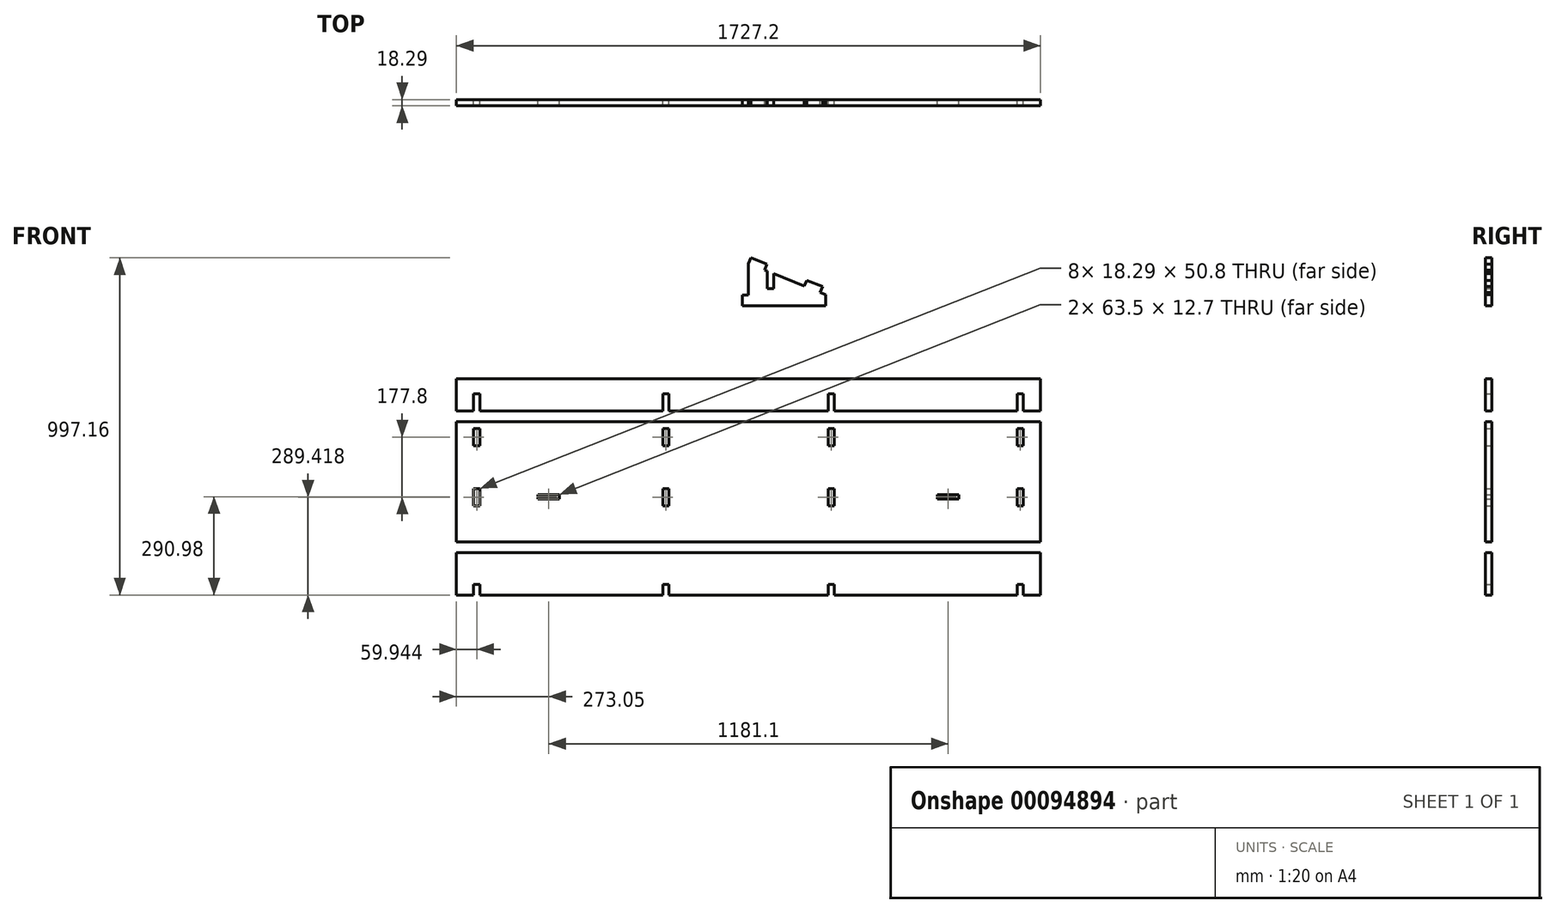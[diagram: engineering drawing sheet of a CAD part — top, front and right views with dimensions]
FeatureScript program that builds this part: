
annotation { "Feature Type Name" : "Feature", "Feature Type Description" : "" }
export const myFeature = defineFeature(function(context is Context, id is Id, definition is map)
    precondition{}
    {
        {
            var Q0;
            Q0=qCreatedBy(makeId("Front.planeOp"),FACE);
            var sketch = newSketch(context, id + "F0", { "sketchPlane" : qUnion([Q0])});
            skLineSegment(sketch, "E0.bottom", {"start": v(-863.6, 177.8) * mm, "end": v(863.6, 177.8) * mm});
            skLineSegment(sketch, "E0.top", {"start": v(-863.6, -177.8) * mm, "end": v(863.6, -177.8) * mm});
            skLineSegment(sketch, "E0.left", {"start": v(-863.6, 177.8) * mm, "end": v(-863.6, -177.8) * mm});
            skLineSegment(sketch, "E0.right", {"start": v(863.6, 177.8) * mm, "end": v(863.6, -177.8) * mm});
            skPoint(sketch, "E0.middle", {"position": v(0, 0) * mm});
            skLineSegment(sketch, "E1.bottom", {"start": v(-914.4, 444.5) * mm, "end": v(914.4, 444.5) * mm});
            skLineSegment(sketch, "E1.top", {"start": v(-914.4, 355.6) * mm, "end": v(914.4, 355.6) * mm});
            skLineSegment(sketch, "E1.left", {"start": v(-914.4, 444.5) * mm, "end": v(-914.4, 355.6) * mm});
            skLineSegment(sketch, "E1.right", {"start": v(914.4, 444.5) * mm, "end": v(914.4, 355.6) * mm});
            skPoint(sketch, "E2", {"position": v(0, 355.6) * mm});
            skLineSegment(sketch, "E3.bottom", {"start": v(0, 355.6) * mm, "end": v(-177.8, 355.6) * mm, "construction": true});
            skLineSegment(sketch, "E3.top", {"start": v(0, 406.4) * mm, "end": v(-177.8, 406.4) * mm, "construction": true});
            skLineSegment(sketch, "E3.left", {"start": v(0, 355.6) * mm, "end": v(0, 406.4) * mm, "construction": true});
            skLineSegment(sketch, "E3.right", {"start": v(-177.8, 355.6) * mm, "end": v(-177.8, 406.4) * mm, "construction": true});
            skLineSegment(sketch, "E4.MirrorCS", {"start": v(0, 406.4) * mm, "end": v(177.8, 406.4) * mm, "construction": true});
            skLineSegment(sketch, "E5.MirrorCS", {"start": v(177.8, 355.6) * mm, "end": v(177.8, 406.4) * mm, "construction": true});
            skLineSegment(sketch, "E6.bottom", {"start": v(177.8, 355.6) * mm, "end": v(482.6, 355.6) * mm});
            skLineSegment(sketch, "E6.top", {"start": v(177.8, 406.4) * mm, "end": v(482.6, 406.4) * mm});
            skLineSegment(sketch, "E6.left", {"start": v(177.8, 355.6) * mm, "end": v(177.8, 406.4) * mm});
            skLineSegment(sketch, "E6.right", {"start": v(482.6, 355.6) * mm, "end": v(482.6, 406.4) * mm});
            skLineSegment(sketch, "E7.bottom", {"start": v(-177.8, 355.6) * mm, "end": v(-482.6, 355.6) * mm});
            skLineSegment(sketch, "E7.top", {"start": v(-177.8, 406.4) * mm, "end": v(-482.6, 406.4) * mm});
            skLineSegment(sketch, "E7.left", {"start": v(-177.8, 355.6) * mm, "end": v(-177.8, 406.4) * mm});
            skLineSegment(sketch, "E7.right", {"start": v(-482.6, 355.6) * mm, "end": v(-482.6, 406.4) * mm});
            skLineSegment(sketch, "E8", {"start": v(0, 645.67) * mm, "end": v(0, 520.7) * mm});
            skLineSegment(sketch, "E9", {"start": v(0, 520.7) * mm, "end": v(228.6, 520.7) * mm});
            skLineSegment(sketch, "E10", {"start": v(228.6, 520.7) * mm, "end": v(228.6, 554.04) * mm});
            skLineSegment(sketch, "E11", {"start": v(228.6, 554.04) * mm, "end": v(0, 645.67) * mm});
            skLineSegment(sketch, "E12", {"start": v(-18.29, 653) * mm, "end": v(311.79, 520.7) * mm, "construction": true});
            skLineSegment(sketch, "E13", {"start": v(0, 645.67) * mm, "end": v(6.8, 662.64) * mm});
            skLineSegment(sketch, "E14", {"start": v(6.8, 662.64) * mm, "end": v(53.96, 643.74) * mm});
            skLineSegment(sketch, "E15", {"start": v(53.96, 643.74) * mm, "end": v(47.15, 626.77) * mm});
            skLineSegment(sketch, "E16.MirrorCS", {"start": v(219, 577.6) * mm, "end": v(171.84, 596.5) * mm});
            skLineSegment(sketch, "E17.MirrorCS", {"start": v(171.84, 596.5) * mm, "end": v(165.04, 579.52) * mm});
            skLineSegment(sketch, "E18.MirrorCS", {"start": v(212.2, 560.62) * mm, "end": v(219, 577.6) * mm});
            skLineSegment(sketch, "E19.0", {"start": v(-863.6, 158.1) * mm, "end": v(863.6, 158.1) * mm, "construction": true});
            skLineSegment(sketch, "E20.0", {"start": v(-863.6, -70.5) * mm, "end": v(863.6, -70.5) * mm, "construction": true});
            skLineSegment(sketch, "E21.bottom", {"start": v(-812.8, 158.1) * mm, "end": v(-794.51, 158.1) * mm});
            skLineSegment(sketch, "E21.top", {"start": v(-812.8, 107.3) * mm, "end": v(-794.51, 107.3) * mm});
            skLineSegment(sketch, "E21.left", {"start": v(-812.8, 158.1) * mm, "end": v(-812.8, 107.3) * mm});
            skLineSegment(sketch, "E21.right", {"start": v(-794.51, 158.1) * mm, "end": v(-794.51, 107.3) * mm});
            skLineSegment(sketch, "E22.0", {"start": v(-253.5, 158.1) * mm, "end": v(-253.5, 107.3) * mm});
            skLineSegment(sketch, "E23.bottom", {"start": v(-253.5, 158.1) * mm, "end": v(-235.2, 158.1) * mm});
            skLineSegment(sketch, "E23.top", {"start": v(-253.5, 107.3) * mm, "end": v(-235.2, 107.3) * mm});
            skLineSegment(sketch, "E23.right", {"start": v(-235.2, 158.1) * mm, "end": v(-235.2, 107.3) * mm});
            skLineSegment(sketch, "E24.MirrorCS", {"start": v(253.5, 107.3) * mm, "end": v(235.2, 107.3) * mm});
            skLineSegment(sketch, "E25.MirrorCS", {"start": v(253.5, 158.1) * mm, "end": v(235.2, 158.1) * mm});
            skLineSegment(sketch, "E26.MirrorCS", {"start": v(812.8, 158.1) * mm, "end": v(794.51, 158.1) * mm});
            skLineSegment(sketch, "E27.MirrorCS", {"start": v(812.8, 107.3) * mm, "end": v(794.51, 107.3) * mm});
            skLineSegment(sketch, "E28.MirrorCS", {"start": v(253.5, 158.1) * mm, "end": v(253.5, 107.3) * mm});
            skLineSegment(sketch, "E29.MirrorCS", {"start": v(794.51, 158.1) * mm, "end": v(794.51, 107.3) * mm});
            skLineSegment(sketch, "E30.MirrorCS", {"start": v(235.2, 158.1) * mm, "end": v(235.2, 107.3) * mm});
            skLineSegment(sketch, "E31.MirrorCS", {"start": v(812.8, 158.1) * mm, "end": v(812.8, 107.3) * mm});
            skLineSegment(sketch, "E32", {"start": v(0, 158.1) * mm, "end": v(0, -70.5) * mm, "construction": true});
            skLineSegment(sketch, "E33", {"start": v(0, 43.8) * mm, "end": v(301.25, 43.8) * mm, "construction": true});
            skLineSegment(sketch, "E34.MirrorCS", {"start": v(-253.5, -70.5) * mm, "end": v(-235.2, -70.5) * mm});
            skLineSegment(sketch, "E35.MirrorCS", {"start": v(-253.5, -19.7) * mm, "end": v(-235.2, -19.7) * mm});
            skLineSegment(sketch, "E36.MirrorCS", {"start": v(253.5, -70.5) * mm, "end": v(235.2, -70.5) * mm});
            skLineSegment(sketch, "E37.MirrorCS", {"start": v(253.5, -19.7) * mm, "end": v(235.2, -19.7) * mm});
            skLineSegment(sketch, "E38.MirrorCS", {"start": v(812.8, -19.7) * mm, "end": v(794.51, -19.7) * mm});
            skLineSegment(sketch, "E39.MirrorCS", {"start": v(-253.5, -70.5) * mm, "end": v(-253.5, -19.7) * mm});
            skLineSegment(sketch, "E40.MirrorCS", {"start": v(-812.8, -70.5) * mm, "end": v(-794.51, -70.5) * mm});
            skLineSegment(sketch, "E41.MirrorCS", {"start": v(812.8, -70.5) * mm, "end": v(794.51, -70.5) * mm});
            skLineSegment(sketch, "E42.MirrorCS", {"start": v(-812.8, -19.7) * mm, "end": v(-794.51, -19.7) * mm});
            skLineSegment(sketch, "E43.MirrorCS", {"start": v(253.5, -70.5) * mm, "end": v(253.5, -19.7) * mm});
            skLineSegment(sketch, "E44.MirrorCS", {"start": v(-794.51, -70.5) * mm, "end": v(-794.51, -19.7) * mm});
            skLineSegment(sketch, "E45.MirrorCS", {"start": v(235.2, -70.5) * mm, "end": v(235.2, -19.7) * mm});
            skLineSegment(sketch, "E46.MirrorCS", {"start": v(794.51, -70.5) * mm, "end": v(794.51, -19.7) * mm});
            skLineSegment(sketch, "E47.MirrorCS", {"start": v(-812.8, -70.5) * mm, "end": v(-812.8, -19.7) * mm});
            skLineSegment(sketch, "E48.MirrorCS", {"start": v(-235.2, -70.5) * mm, "end": v(-235.2, -19.7) * mm});
            skLineSegment(sketch, "E49.MirrorCS", {"start": v(812.8, -70.5) * mm, "end": v(812.8, -19.7) * mm});
            skLineSegment(sketch, "E50.bottom", {"start": v(55.86, 571.5) * mm, "end": v(74.14, 571.5) * mm});
            skLineSegment(sketch, "E50.top", {"start": v(55.86, 615.95) * mm, "end": v(74.14, 615.95) * mm, "construction": true});
            skLineSegment(sketch, "E50.left", {"start": v(55.86, 571.5) * mm, "end": v(55.86, 615.95) * mm});
            skLineSegment(sketch, "E50.right", {"start": v(74.14, 571.5) * mm, "end": v(74.14, 615.95) * mm});
            skLineSegment(sketch, "E51", {"start": v(55.86, 615.95) * mm, "end": v(55.86, 623.28) * mm});
            skLineSegment(sketch, "E52.bottom", {"start": v(-863.6, 209.55) * mm, "end": v(863.6, 209.55) * mm});
            skLineSegment(sketch, "E52.top", {"start": v(-863.6, 304.8) * mm, "end": v(863.6, 304.8) * mm});
            skLineSegment(sketch, "E52.left", {"start": v(-863.6, 209.55) * mm, "end": v(-863.6, 304.8) * mm});
            skLineSegment(sketch, "E52.right", {"start": v(863.6, 209.55) * mm, "end": v(863.6, 304.8) * mm});
            skLineSegment(sketch, "E53.bottom", {"start": v(-812.8, 209.55) * mm, "end": v(-794.51, 209.55) * mm});
            skLineSegment(sketch, "E53.top", {"start": v(-812.8, 260.35) * mm, "end": v(-794.51, 260.35) * mm});
            skLineSegment(sketch, "E53.left", {"start": v(-812.8, 209.55) * mm, "end": v(-812.8, 260.35) * mm});
            skLineSegment(sketch, "E53.right", {"start": v(-794.51, 209.55) * mm, "end": v(-794.51, 260.35) * mm});
            skLineSegment(sketch, "E54.bottom", {"start": v(-253.5, 209.55) * mm, "end": v(-235.2, 209.55) * mm});
            skLineSegment(sketch, "E54.top", {"start": v(-253.5, 260.35) * mm, "end": v(-235.2, 260.35) * mm});
            skLineSegment(sketch, "E54.left", {"start": v(-253.5, 209.55) * mm, "end": v(-253.5, 260.35) * mm});
            skLineSegment(sketch, "E54.right", {"start": v(-235.2, 209.55) * mm, "end": v(-235.2, 260.35) * mm});
            skLineSegment(sketch, "E55.MirrorCS", {"start": v(812.8, 209.55) * mm, "end": v(794.51, 209.55) * mm});
            skLineSegment(sketch, "E56.MirrorCS", {"start": v(235.2, 209.55) * mm, "end": v(235.2, 260.35) * mm});
            skLineSegment(sketch, "E57.MirrorCS", {"start": v(812.8, 260.35) * mm, "end": v(794.51, 260.35) * mm});
            skLineSegment(sketch, "E58.MirrorCS", {"start": v(253.5, 209.55) * mm, "end": v(253.5, 260.35) * mm});
            skLineSegment(sketch, "E59.MirrorCS", {"start": v(253.5, 260.35) * mm, "end": v(235.2, 260.35) * mm});
            skLineSegment(sketch, "E60.MirrorCS", {"start": v(253.5, 209.55) * mm, "end": v(235.2, 209.55) * mm});
            skLineSegment(sketch, "E61.MirrorCS", {"start": v(794.51, 209.55) * mm, "end": v(794.51, 260.35) * mm});
            skLineSegment(sketch, "E62.MirrorCS", {"start": v(812.8, 209.55) * mm, "end": v(812.8, 260.35) * mm});
            skLineSegment(sketch, "E63.bottom", {"start": v(0, 520.7) * mm, "end": v(-18.29, 520.7) * mm});
            skLineSegment(sketch, "E63.top", {"start": v(0, 552.45) * mm, "end": v(-18.29, 552.45) * mm});
            skLineSegment(sketch, "E63.left", {"start": v(0, 520.7) * mm, "end": v(0, 552.45) * mm});
            skLineSegment(sketch, "E63.right", {"start": v(-18.29, 520.7) * mm, "end": v(-18.29, 552.45) * mm});
            skLineSegment(sketch, "E64", {"start": v(0, 583.18) * mm, "end": v(305.15, 583.18) * mm, "construction": true});
            skLineSegment(sketch, "E65", {"start": v(205.05, 583.18) * mm, "end": v(198.24, 566.2) * mm, "construction": true});
            skLineSegment(sketch, "E66.0", {"start": v(188.07, 589.99) * mm, "end": v(181.27, 573.01) * mm});
            skLineSegment(sketch, "E67", {"start": v(6.8, 662.64) * mm, "end": v(188.07, 589.99) * mm, "construction": true});
            skLineSegment(sketch, "E68", {"start": v(0, 158.1) * mm, "end": v(0, -37.2) * mm, "construction": true});
            skLineSegment(sketch, "E69", {"start": v(0, -37.2) * mm, "end": v(-907.94, -37.2) * mm, "construction": true});
            skLineSegment(sketch, "E70.0", {"start": v(0, -49.9) * mm, "end": v(-590.55, -49.9) * mm, "construction": true});
            skLineSegment(sketch, "E71.bottom", {"start": v(-558.8, -49.9) * mm, "end": v(-622.3, -49.9) * mm});
            skLineSegment(sketch, "E71.top", {"start": v(-558.8, -37.2) * mm, "end": v(-622.3, -37.2) * mm});
            skLineSegment(sketch, "E71.left", {"start": v(-558.8, -49.9) * mm, "end": v(-558.8, -37.2) * mm});
            skLineSegment(sketch, "E71.right", {"start": v(-622.3, -49.9) * mm, "end": v(-622.3, -37.2) * mm});
            skPoint(sketch, "E71.middle", {"position": v(-590.55, -43.54) * mm});
            skPoint(sketch, "E72.MirrorP", {"position": v(590.55, -43.54) * mm});
            skLineSegment(sketch, "E73.MirrorCS", {"start": v(558.8, -49.9) * mm, "end": v(622.3, -49.9) * mm});
            skLineSegment(sketch, "E74.MirrorCS", {"start": v(558.8, -37.2) * mm, "end": v(622.3, -37.2) * mm});
            skLineSegment(sketch, "E75.MirrorCS", {"start": v(558.8, -49.9) * mm, "end": v(558.8, -37.2) * mm});
            skLineSegment(sketch, "E76.MirrorCS", {"start": v(622.3, -49.9) * mm, "end": v(622.3, -37.2) * mm});
            skLineSegment(sketch, "E77", {"start": v(-18.29, 653) * mm, "end": v(-10.32, 672.87) * mm, "construction": true});
            skLineSegment(sketch, "E78", {"start": v(6.8, 662.64) * mm, "end": v(-11.48, 669.97) * mm, "construction": true});
            skLineSegment(sketch, "E79", {"start": v(0, 158.1) * mm, "end": v(0, 177.8) * mm, "construction": true});
            skLineSegment(sketch, "E80", {"start": v(-18.29, 552.45) * mm, "end": v(-18.29, 645.67) * mm, "construction": true});
            skLineSegment(sketch, "E81.bottom", {"start": v(-863.6, -209.55) * mm, "end": v(863.6, -209.55) * mm});
            skLineSegment(sketch, "E81.top", {"start": v(-863.6, -334.52) * mm, "end": v(863.6, -334.52) * mm});
            skLineSegment(sketch, "E81.left", {"start": v(-863.6, -209.55) * mm, "end": v(-863.6, -334.52) * mm});
            skLineSegment(sketch, "E81.right", {"start": v(863.6, -209.55) * mm, "end": v(863.6, -334.52) * mm});
            skLineSegment(sketch, "E82.bottom", {"start": v(-812.8, -334.52) * mm, "end": v(-794.51, -334.52) * mm});
            skLineSegment(sketch, "E82.top", {"start": v(-812.8, -302.77) * mm, "end": v(-794.51, -302.77) * mm});
            skLineSegment(sketch, "E82.left", {"start": v(-812.8, -334.52) * mm, "end": v(-812.8, -302.77) * mm});
            skLineSegment(sketch, "E82.right", {"start": v(-794.51, -334.52) * mm, "end": v(-794.51, -302.77) * mm});
            skLineSegment(sketch, "E83.bottom", {"start": v(-253.5, -334.52) * mm, "end": v(-235.2, -334.52) * mm});
            skLineSegment(sketch, "E83.top", {"start": v(-253.5, -302.77) * mm, "end": v(-235.2, -302.77) * mm});
            skLineSegment(sketch, "E83.left", {"start": v(-253.5, -334.52) * mm, "end": v(-253.5, -302.77) * mm});
            skLineSegment(sketch, "E83.right", {"start": v(-235.2, -334.52) * mm, "end": v(-235.2, -302.77) * mm});
            skLineSegment(sketch, "E84.bottom", {"start": v(235.2, -334.52) * mm, "end": v(253.5, -334.52) * mm});
            skLineSegment(sketch, "E84.top", {"start": v(235.2, -302.77) * mm, "end": v(253.5, -302.77) * mm});
            skLineSegment(sketch, "E84.left", {"start": v(235.2, -334.52) * mm, "end": v(235.2, -302.77) * mm});
            skLineSegment(sketch, "E84.right", {"start": v(253.5, -334.52) * mm, "end": v(253.5, -302.77) * mm});
            skLineSegment(sketch, "E85.bottom", {"start": v(794.51, -334.52) * mm, "end": v(812.8, -334.52) * mm});
            skLineSegment(sketch, "E85.top", {"start": v(794.51, -302.77) * mm, "end": v(812.8, -302.77) * mm});
            skLineSegment(sketch, "E85.left", {"start": v(794.51, -334.52) * mm, "end": v(794.51, -302.77) * mm});
            skLineSegment(sketch, "E85.right", {"start": v(812.8, -334.52) * mm, "end": v(812.8, -302.77) * mm});
            skLineSegment(sketch, "E86", {"start": v(-794.51, -302.77) * mm, "end": v(-794.51, -209.55) * mm, "construction": true});
            skSolve(sketch);
        }
        {
            var Q0;
            {var subQ7=sQuery(id+"F0.wireOp",EDGE,"E8");Q0=makeQuery(id+"F0.imprint","IMPRINT",FACE,{"disambiguationData":[TD([[makeQuery(id+"F0.imprint","IMPRINT",EDGE,{"derivedFrom":subQ7}),1.0]])]});}
            var Q1;
            {var subQ0=sQuery(id+"F0.wireOp",EDGE,"E13");Q1=makeQuery(id+"F0.imprint","IMPRINT",FACE,{"disambiguationData":[TD([[makeQuery(id+"F0.imprint","IMPRINT",EDGE,{"derivedFrom":subQ0}),-1.0]])]});}
            var Q2;
            Q2=makeQuery(id+"F0.imprint","IMPRINT",FACE,{"disambiguationData":[TD([[makeQuery(id+"F0.imprint","IMPRINT",EDGE,{"derivedFrom":sQuery(id+"F0.wireOp",EDGE,"E16.MirrorCS")}),1.0]])]});
            var Q3;
            Q3=makeQuery(id+"F0.imprint","IMPRINT",FACE,{"disambiguationData":[TD([[makeQuery(id+"F0.imprint","IMPRINT",EDGE,{"derivedFrom":sQuery(id+"F0.wireOp",EDGE,"E52.top")}),-1.0]])]});
            var Q4;
            Q4=makeQuery(id+"F0.imprint","IMPRINT",FACE,{"disambiguationData":[TD([[makeQuery(id+"F0.imprint","IMPRINT",EDGE,{"derivedFrom":sQuery(id+"F0.wireOp",EDGE,"E0.bottom")}),-1.0]])]});
            var Q5;
            Q5=makeQuery(id+"F0.imprint","IMPRINT",FACE,{"disambiguationData":[TD([[makeQuery(id+"F0.imprint","IMPRINT",EDGE,{"derivedFrom":sQuery(id+"F0.wireOp",EDGE,"E63.bottom")}),-1.0]])]});
            var Q6;
            Q6=makeQuery(id+"F0.imprint","IMPRINT",FACE,{"disambiguationData":[TD([[makeQuery(id+"F0.imprint","IMPRINT",EDGE,{"derivedFrom":sQuery(id+"F0.wireOp",EDGE,"E81.bottom")}),-1.0]])]});
            extrude(context, id + "F1", {"entities" : qUnion([Q0, Q1, Q2, Q3, Q4, Q5, Q6]), "depth" : 18.29 * mm});
        }
    });
